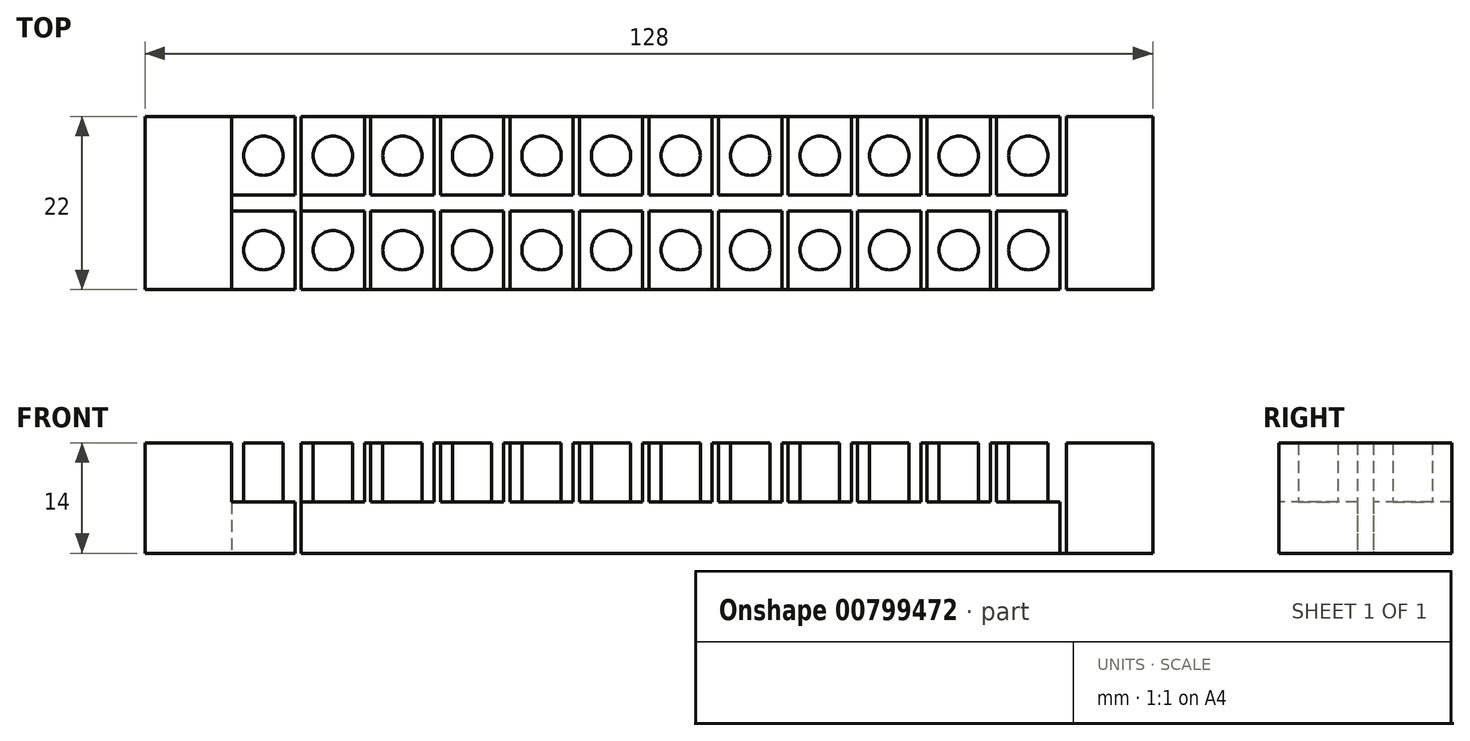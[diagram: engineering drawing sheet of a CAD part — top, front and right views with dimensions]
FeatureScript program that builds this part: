
annotation { "Feature Type Name" : "Feature", "Feature Type Description" : "" }
export const myFeature = defineFeature(function(context is Context, id is Id, definition is map)
    precondition{}
    {
        {
            var Q0;
            Q0=qCreatedBy(makeId("Top.planeOp"),FACE);
            var sketch = newSketch(context, id + "F0", { "sketchPlane" : qUnion([Q0])});
            skLineSegment(sketch, "E0.bottom", {"start": v(0, 0) * mm, "end": v(128, 0) * mm});
            skLineSegment(sketch, "E0.top", {"start": v(0, 22) * mm, "end": v(128, 22) * mm});
            skLineSegment(sketch, "E0.left", {"start": v(0, 0) * mm, "end": v(0, 22) * mm});
            skLineSegment(sketch, "E0.right", {"start": v(128, 0) * mm, "end": v(128, 22) * mm});
            skLineSegment(sketch, "E1", {"start": v(11, 22) * mm, "end": v(11, 0) * mm});
            skLineSegment(sketch, "E2", {"start": v(117, 22) * mm, "end": v(117, 12) * mm});
            skLineSegment(sketch, "E3.0", {"start": v(11, 12) * mm, "end": v(19.03, 12) * mm});
            skLineSegment(sketch, "E4.0", {"start": v(11, 10) * mm, "end": v(19.03, 10) * mm});
            skLineSegment(sketch, "E5.0", {"start": v(19.03, 22) * mm, "end": v(19.03, 12) * mm});
            skCircle(sketch, "E6", {"center": v(15.02, 17) * mm, "radius": 2.5 * mm});
            skLineSegment(sketch, "E7.trimOffspring", {"start": v(19.83, 12) * mm, "end": v(117, 12) * mm});
            skLineSegment(sketch, "E8.trimOffspring", {"start": v(19.03, 10) * mm, "end": v(19.03, 0) * mm});
            skLineSegment(sketch, "E9.trimOffspring", {"start": v(20.63, 10) * mm, "end": v(117, 10) * mm});
            skCircle(sketch, "E10.1.0.0", {"center": v(23.85, 17) * mm, "radius": 2.5 * mm});
            skLineSegment(sketch, "E10.1.0.1", {"start": v(27.87, 22) * mm, "end": v(27.87, 12) * mm});
            skLineSegment(sketch, "E10.1.0.2", {"start": v(19.83, 22) * mm, "end": v(19.83, 12) * mm});
            skCircle(sketch, "E10.2.0.0", {"center": v(32.68, 17) * mm, "radius": 2.5 * mm});
            skLineSegment(sketch, "E10.2.0.1", {"start": v(36.7, 22) * mm, "end": v(36.7, 12) * mm});
            skLineSegment(sketch, "E10.2.0.2", {"start": v(28.67, 22) * mm, "end": v(28.67, 0) * mm});
            skCircle(sketch, "E10.3.0.0", {"center": v(41.52, 17) * mm, "radius": 2.5 * mm});
            skLineSegment(sketch, "E10.3.0.1", {"start": v(45.53, 22) * mm, "end": v(45.53, 12) * mm});
            skLineSegment(sketch, "E10.3.0.2", {"start": v(37.5, 22) * mm, "end": v(37.5, 12) * mm});
            skCircle(sketch, "E10.4.0.0", {"center": v(50.35, 17) * mm, "radius": 2.5 * mm});
            skLineSegment(sketch, "E10.4.0.1", {"start": v(54.37, 22) * mm, "end": v(54.37, 12) * mm});
            skLineSegment(sketch, "E10.4.0.2", {"start": v(46.33, 22) * mm, "end": v(46.33, 12) * mm});
            skCircle(sketch, "E10.5.0.0", {"center": v(59.18, 17) * mm, "radius": 2.5 * mm});
            skLineSegment(sketch, "E10.5.0.1", {"start": v(63.2, 22) * mm, "end": v(63.2, 12) * mm});
            skLineSegment(sketch, "E10.5.0.2", {"start": v(55.17, 22) * mm, "end": v(55.17, 12) * mm});
            skCircle(sketch, "E10.6.0.0", {"center": v(68.01, 17) * mm, "radius": 2.5 * mm});
            skLineSegment(sketch, "E10.6.0.1", {"start": v(72.03, 22) * mm, "end": v(72.03, 12) * mm});
            skLineSegment(sketch, "E10.6.0.2", {"start": v(64, 22) * mm, "end": v(64, 12) * mm});
            skCircle(sketch, "E10.7.0.0", {"center": v(76.85, 17) * mm, "radius": 2.5 * mm});
            skLineSegment(sketch, "E10.7.0.1", {"start": v(80.86, 22) * mm, "end": v(80.86, 12) * mm});
            skLineSegment(sketch, "E10.7.0.2", {"start": v(72.83, 22) * mm, "end": v(72.83, 12) * mm});
            skCircle(sketch, "E10.8.0.0", {"center": v(85.68, 17) * mm, "radius": 2.5 * mm});
            skLineSegment(sketch, "E10.8.0.1", {"start": v(89.7, 22) * mm, "end": v(89.7, 12) * mm});
            skLineSegment(sketch, "E10.8.0.2", {"start": v(81.66, 22) * mm, "end": v(81.66, 12) * mm});
            skCircle(sketch, "E10.9.0.0", {"center": v(94.51, 17) * mm, "radius": 2.5 * mm});
            skLineSegment(sketch, "E10.9.0.1", {"start": v(98.53, 22) * mm, "end": v(98.53, 12) * mm});
            skLineSegment(sketch, "E10.9.0.2", {"start": v(90.5, 22) * mm, "end": v(90.5, 12) * mm});
            skCircle(sketch, "E10.10.0.0", {"center": v(103.35, 17) * mm, "radius": 2.5 * mm});
            skLineSegment(sketch, "E10.10.0.1", {"start": v(107.36, 22) * mm, "end": v(107.36, 12) * mm});
            skLineSegment(sketch, "E10.10.0.2", {"start": v(99.33, 22) * mm, "end": v(99.33, 12) * mm});
            skCircle(sketch, "E10.11.0.0", {"center": v(112.18, 17) * mm, "radius": 2.5 * mm});
            skLineSegment(sketch, "E10.11.0.1", {"start": v(116.2, 22) * mm, "end": v(116.2, 12) * mm});
            skLineSegment(sketch, "E10.11.0.2", {"start": v(108.16, 22) * mm, "end": v(108.16, 12) * mm});
            skLineSegment(sketch, "E10.direction1", {"start": v(11, 0) * mm, "end": v(19.83, 0) * mm, "construction": true});
            skCircle(sketch, "E11", {"center": v(15.02, 5) * mm, "radius": 2.5 * mm});
            skLineSegment(sketch, "E12.1.0.0", {"start": v(19.83, 22) * mm, "end": v(19.83, 0) * mm});
            skCircle(sketch, "E12.1.0.1", {"center": v(23.85, 5) * mm, "radius": 2.5 * mm});
            skLineSegment(sketch, "E12.1.0.2", {"start": v(27.87, 10) * mm, "end": v(27.87, 0) * mm});
            skLineSegment(sketch, "E12.2.0.0", {"start": v(28.67, 22) * mm, "end": v(28.67, 12) * mm});
            skCircle(sketch, "E12.2.0.1", {"center": v(32.68, 5) * mm, "radius": 2.5 * mm});
            skLineSegment(sketch, "E12.2.0.2", {"start": v(36.7, 10) * mm, "end": v(36.7, 0) * mm});
            skLineSegment(sketch, "E13.0.3.0", {"start": v(37.5, 22) * mm, "end": v(37.5, 0) * mm});
            skCircle(sketch, "E13.3.3.0", {"center": v(41.52, 5) * mm, "radius": 2.5 * mm});
            skLineSegment(sketch, "E13.5.3.0", {"start": v(45.53, 10) * mm, "end": v(45.53, 0) * mm});
            skCircle(sketch, "E13.3.4.0", {"center": v(50.35, 5) * mm, "radius": 2.5 * mm});
            skLineSegment(sketch, "E13.5.4.0", {"start": v(54.37, 10) * mm, "end": v(54.37, 0) * mm});
            skCircle(sketch, "E13.3.5.0", {"center": v(59.18, 5) * mm, "radius": 2.5 * mm});
            skLineSegment(sketch, "E13.5.5.0", {"start": v(63.2, 10) * mm, "end": v(63.2, 0) * mm});
            skCircle(sketch, "E13.3.6.0", {"center": v(68.02, 5) * mm, "radius": 2.5 * mm});
            skLineSegment(sketch, "E13.5.6.0", {"start": v(72.03, 10) * mm, "end": v(72.03, 0) * mm});
            skCircle(sketch, "E13.3.7.0", {"center": v(76.85, 5) * mm, "radius": 2.5 * mm});
            skLineSegment(sketch, "E13.5.7.0", {"start": v(80.87, 10) * mm, "end": v(80.87, 0) * mm});
            skLineSegment(sketch, "E13.0.8.0", {"start": v(81.67, 22) * mm, "end": v(81.67, 12) * mm});
            skCircle(sketch, "E13.3.8.0", {"center": v(85.68, 5) * mm, "radius": 2.5 * mm});
            skLineSegment(sketch, "E13.5.8.0", {"start": v(89.7, 10) * mm, "end": v(89.7, 0) * mm});
            skCircle(sketch, "E13.3.9.0", {"center": v(94.52, 5) * mm, "radius": 2.5 * mm});
            skLineSegment(sketch, "E13.5.9.0", {"start": v(98.53, 10) * mm, "end": v(98.53, 0) * mm});
            skCircle(sketch, "E13.3.10.0", {"center": v(103.35, 5) * mm, "radius": 2.5 * mm});
            skLineSegment(sketch, "E13.5.10.0", {"start": v(107.37, 10) * mm, "end": v(107.37, 0) * mm});
            skLineSegment(sketch, "E13.0.11.0", {"start": v(108.17, 22) * mm, "end": v(108.17, 12) * mm});
            skCircle(sketch, "E13.3.11.0", {"center": v(112.18, 5) * mm, "radius": 2.5 * mm});
            skLineSegment(sketch, "E13.5.11.0", {"start": v(116.2, 10) * mm, "end": v(116.2, 0) * mm});
            skLineSegment(sketch, "E14.trimOffspring", {"start": v(19.83, 10) * mm, "end": v(19.83, 0) * mm});
            skLineSegment(sketch, "E15.trimOffspring", {"start": v(28.67, 10) * mm, "end": v(28.67, 0) * mm});
            skLineSegment(sketch, "E16.trimOffspring", {"start": v(37.5, 10) * mm, "end": v(37.5, 0) * mm});
            skLineSegment(sketch, "E17.trimOffspring", {"start": v(46.33, 10) * mm, "end": v(46.33, 0) * mm});
            skLineSegment(sketch, "E18.trimOffspring", {"start": v(55.17, 10) * mm, "end": v(55.17, 0) * mm});
            skLineSegment(sketch, "E19.trimOffspring", {"start": v(117, 10) * mm, "end": v(117, 0) * mm});
            skLineSegment(sketch, "E20.trimOffspring", {"start": v(108.16, 10) * mm, "end": v(108.16, 0) * mm});
            skLineSegment(sketch, "E21.trimOffspring", {"start": v(99.33, 10) * mm, "end": v(99.33, 0) * mm});
            skLineSegment(sketch, "E22.trimOffspring", {"start": v(108.17, 10) * mm, "end": v(108.17, 0) * mm});
            skLineSegment(sketch, "E23.trimOffspring", {"start": v(81.67, 10) * mm, "end": v(81.67, 0) * mm});
            skLineSegment(sketch, "E24.trimOffspring", {"start": v(90.5, 10) * mm, "end": v(90.5, 0) * mm});
            skLineSegment(sketch, "E25.trimOffspring", {"start": v(72.83, 10) * mm, "end": v(72.83, 0) * mm});
            skLineSegment(sketch, "E26.trimOffspring", {"start": v(81.66, 10) * mm, "end": v(81.66, 0) * mm});
            skLineSegment(sketch, "E27.trimOffspring", {"start": v(64, 10) * mm, "end": v(64, 0) * mm});
            skLineSegment(sketch, "E28.trimOffspring", {"start": v(19.83, 10) * mm, "end": v(20.63, 10) * mm});
            skSolve(sketch);
        }
        {
            var Q0;
            {var subQ4=sQuery(id+"F0.wireOp",EDGE,"E0.left");Q0=makeQuery(id+"F0.imprint","IMPRINT",FACE,{"disambiguationData":[TD([[makeQuery(id+"F0.imprint","IMPRINT",EDGE,{"derivedFrom":subQ4}),-1.0]])]});}
            var Q1;
            {var subQ4=sQuery(id+"F0.wireOp",EDGE,"E3.0");Q1=makeQuery(id+"F0.imprint","IMPRINT",FACE,{"disambiguationData":[TD([[makeQuery(id+"F0.imprint","IMPRINT",EDGE,{"derivedFrom":subQ4}),-1.0]])]});}
            var Q2;
            {var subQ0=sQuery(id+"F0.wireOp",EDGE,"E5.0");Q2=makeQuery(id+"F0.imprint","IMPRINT",FACE,{"disambiguationData":[TD([[makeQuery(id+"F0.imprint","IMPRINT",EDGE,{"derivedFrom":subQ0}),1.0]])]});}
            var Q3;
            {var subQ0=sQuery(id+"F0.wireOp",EDGE,"E8.trimOffspring");Q3=makeQuery(id+"F0.imprint","IMPRINT",FACE,{"disambiguationData":[TD([[makeQuery(id+"F0.imprint","IMPRINT",EDGE,{"derivedFrom":subQ0}),1.0]])]});}
            var Q4;
            {var subQ4=sQuery(id+"F0.wireOp",EDGE,"E7.trimOffspring");var subQ5=makeQuery(id+"F0.imprint","INTERSECT",VERTEX,{"derivedFrom":[subQ4,sQuery(id+"F0.wireOp",EDGE,"E10.1.0.1")]});Q4=makeQuery(id+"F0.imprint","IMPRINT",FACE,{"disambiguationData":[TD([[makeQuery(id+"F0.imprint","IMPRINT",EDGE,{"disambiguationData":[TD([[subQ5,1.0]])],"derivedFrom":subQ4}),-1.0]])]});}
            var Q5;
            {var subQ0=sQuery(id+"F0.wireOp",EDGE,"E10.1.0.1");Q5=makeQuery(id+"F0.imprint","IMPRINT",FACE,{"disambiguationData":[TD([[makeQuery(id+"F0.imprint","IMPRINT",EDGE,{"derivedFrom":subQ0}),1.0]])]});}
            var Q6;
            {var subQ3=sQuery(id+"F0.wireOp",EDGE,"E12.1.0.2");Q6=makeQuery(id+"F0.imprint","IMPRINT",FACE,{"disambiguationData":[TD([[makeQuery(id+"F0.imprint","IMPRINT",EDGE,{"derivedFrom":subQ3}),1.0]])]});}
            var Q7;
            {var subQ0=sQuery(id+"F0.wireOp",EDGE,"E7.trimOffspring");var subQ9=makeQuery(id+"F0.imprint","INTERSECT",VERTEX,{"derivedFrom":[subQ0,sQuery(id+"F0.wireOp",EDGE,"E12.2.0.0")]});Q7=makeQuery(id+"F0.imprint","IMPRINT",FACE,{"disambiguationData":[TD([[makeQuery(id+"F0.imprint","IMPRINT",EDGE,{"disambiguationData":[TD([[subQ9,1.0]])],"derivedFrom":subQ0}),-1.0]])]});}
            var Q8;
            {var subQ0=sQuery(id+"F0.wireOp",EDGE,"E10.2.0.1");Q8=makeQuery(id+"F0.imprint","IMPRINT",FACE,{"disambiguationData":[TD([[makeQuery(id+"F0.imprint","IMPRINT",EDGE,{"derivedFrom":subQ0}),1.0]])]});}
            var Q9;
            {var subQ0=sQuery(id+"F0.wireOp",EDGE,"E12.2.0.2");Q9=makeQuery(id+"F0.imprint","IMPRINT",FACE,{"disambiguationData":[TD([[makeQuery(id+"F0.imprint","IMPRINT",EDGE,{"derivedFrom":subQ0}),1.0]])]});}
            var Q10;
            {var subQ4=sQuery(id+"F0.wireOp",EDGE,"E7.trimOffspring");var subQ5=makeQuery(id+"F0.imprint","INTERSECT",VERTEX,{"derivedFrom":[subQ4,sQuery(id+"F0.wireOp",EDGE,"E10.3.0.1")]});Q10=makeQuery(id+"F0.imprint","IMPRINT",FACE,{"disambiguationData":[TD([[makeQuery(id+"F0.imprint","IMPRINT",EDGE,{"disambiguationData":[TD([[subQ5,1.0]])],"derivedFrom":subQ4}),-1.0]])]});}
            var Q11;
            {var subQ0=sQuery(id+"F0.wireOp",EDGE,"E10.3.0.1");Q11=makeQuery(id+"F0.imprint","IMPRINT",FACE,{"disambiguationData":[TD([[makeQuery(id+"F0.imprint","IMPRINT",EDGE,{"derivedFrom":subQ0}),1.0]])]});}
            var Q12;
            {var subQ0=sQuery(id+"F0.wireOp",EDGE,"E13.5.3.0");Q12=makeQuery(id+"F0.imprint","IMPRINT",FACE,{"disambiguationData":[TD([[makeQuery(id+"F0.imprint","IMPRINT",EDGE,{"derivedFrom":subQ0}),1.0]])]});}
            var Q13;
            {var subQ4=sQuery(id+"F0.wireOp",EDGE,"E7.trimOffspring");var subQ5=makeQuery(id+"F0.imprint","INTERSECT",VERTEX,{"derivedFrom":[subQ4,sQuery(id+"F0.wireOp",EDGE,"E10.4.0.1")]});Q13=makeQuery(id+"F0.imprint","IMPRINT",FACE,{"disambiguationData":[TD([[makeQuery(id+"F0.imprint","IMPRINT",EDGE,{"disambiguationData":[TD([[subQ5,1.0]])],"derivedFrom":subQ4}),-1.0]])]});}
            var Q14;
            {var subQ0=sQuery(id+"F0.wireOp",EDGE,"E10.4.0.1");Q14=makeQuery(id+"F0.imprint","IMPRINT",FACE,{"disambiguationData":[TD([[makeQuery(id+"F0.imprint","IMPRINT",EDGE,{"derivedFrom":subQ0}),1.0]])]});}
            var Q15;
            {var subQ0=sQuery(id+"F0.wireOp",EDGE,"E13.5.4.0");Q15=makeQuery(id+"F0.imprint","IMPRINT",FACE,{"disambiguationData":[TD([[makeQuery(id+"F0.imprint","IMPRINT",EDGE,{"derivedFrom":subQ0}),1.0]])]});}
            var Q16;
            {var subQ4=sQuery(id+"F0.wireOp",EDGE,"E7.trimOffspring");var subQ5=makeQuery(id+"F0.imprint","INTERSECT",VERTEX,{"derivedFrom":[subQ4,sQuery(id+"F0.wireOp",EDGE,"E10.5.0.1")]});Q16=makeQuery(id+"F0.imprint","IMPRINT",FACE,{"disambiguationData":[TD([[makeQuery(id+"F0.imprint","IMPRINT",EDGE,{"disambiguationData":[TD([[subQ5,1.0]])],"derivedFrom":subQ4}),-1.0]])]});}
            var Q17;
            {var subQ0=sQuery(id+"F0.wireOp",EDGE,"E10.5.0.1");Q17=makeQuery(id+"F0.imprint","IMPRINT",FACE,{"disambiguationData":[TD([[makeQuery(id+"F0.imprint","IMPRINT",EDGE,{"derivedFrom":subQ0}),1.0]])]});}
            var Q18;
            {var subQ3=sQuery(id+"F0.wireOp",EDGE,"E13.5.5.0");Q18=makeQuery(id+"F0.imprint","IMPRINT",FACE,{"disambiguationData":[TD([[makeQuery(id+"F0.imprint","IMPRINT",EDGE,{"derivedFrom":subQ3}),1.0]])]});}
            var Q19;
            {var subQ3=sQuery(id+"F0.wireOp",EDGE,"E0.right");Q19=makeQuery(id+"F0.imprint","IMPRINT",FACE,{"disambiguationData":[TD([[makeQuery(id+"F0.imprint","IMPRINT",EDGE,{"derivedFrom":subQ3}),1.0]])]});}
            var Q20;
            {var subQ0=sQuery(id+"F0.wireOp",EDGE,"E10.6.0.1");Q20=makeQuery(id+"F0.imprint","IMPRINT",FACE,{"disambiguationData":[TD([[makeQuery(id+"F0.imprint","IMPRINT",EDGE,{"derivedFrom":subQ0}),1.0]])]});}
            var Q21;
            {var subQ0=sQuery(id+"F0.wireOp",EDGE,"E13.5.6.0");Q21=makeQuery(id+"F0.imprint","IMPRINT",FACE,{"disambiguationData":[TD([[makeQuery(id+"F0.imprint","IMPRINT",EDGE,{"derivedFrom":subQ0}),1.0]])]});}
            var Q22;
            {var subQ0=sQuery(id+"F0.wireOp",EDGE,"E10.7.0.1");Q22=makeQuery(id+"F0.imprint","IMPRINT",FACE,{"disambiguationData":[TD([[makeQuery(id+"F0.imprint","IMPRINT",EDGE,{"derivedFrom":subQ0}),1.0]])]});}
            var Q23;
            {var subQ0=sQuery(id+"F0.wireOp",EDGE,"E10.8.0.1");Q23=makeQuery(id+"F0.imprint","IMPRINT",FACE,{"disambiguationData":[TD([[makeQuery(id+"F0.imprint","IMPRINT",EDGE,{"derivedFrom":subQ0}),1.0]])]});}
            var Q24;
            {var subQ0=sQuery(id+"F0.wireOp",EDGE,"E10.9.0.1");Q24=makeQuery(id+"F0.imprint","IMPRINT",FACE,{"disambiguationData":[TD([[makeQuery(id+"F0.imprint","IMPRINT",EDGE,{"derivedFrom":subQ0}),1.0]])]});}
            var Q25;
            {var subQ0=sQuery(id+"F0.wireOp",EDGE,"E13.5.7.0");Q25=makeQuery(id+"F0.imprint","IMPRINT",FACE,{"disambiguationData":[TD([[makeQuery(id+"F0.imprint","IMPRINT",EDGE,{"derivedFrom":subQ0}),1.0]])]});}
            var Q26;
            {var subQ0=sQuery(id+"F0.wireOp",EDGE,"E13.5.8.0");Q26=makeQuery(id+"F0.imprint","IMPRINT",FACE,{"disambiguationData":[TD([[makeQuery(id+"F0.imprint","IMPRINT",EDGE,{"derivedFrom":subQ0}),1.0]])]});}
            var Q27;
            {var subQ0=sQuery(id+"F0.wireOp",EDGE,"E13.5.9.0");Q27=makeQuery(id+"F0.imprint","IMPRINT",FACE,{"disambiguationData":[TD([[makeQuery(id+"F0.imprint","IMPRINT",EDGE,{"derivedFrom":subQ0}),1.0]])]});}
            var Q28;
            {var subQ0=sQuery(id+"F0.wireOp",EDGE,"E13.5.10.0");Q28=makeQuery(id+"F0.imprint","IMPRINT",FACE,{"disambiguationData":[TD([[makeQuery(id+"F0.imprint","IMPRINT",EDGE,{"derivedFrom":subQ0}),1.0]])]});}
            var Q29;
            {var subQ0=sQuery(id+"F0.wireOp",EDGE,"E10.10.0.1");Q29=makeQuery(id+"F0.imprint","IMPRINT",FACE,{"disambiguationData":[TD([[makeQuery(id+"F0.imprint","IMPRINT",EDGE,{"derivedFrom":subQ0}),1.0]])]});}
            extrude(context, id + "F1", {"entities" : qUnion([Q0, Q1, Q2, Q3, Q4, Q5, Q6, Q7, Q8, Q9, Q10, Q11, Q12, Q13, Q14, Q15, Q16, Q17, Q18, Q19, Q20, Q21, Q22, Q23, Q24, Q25, Q26, Q27, Q28, Q29]), "depth" : 14 * mm, "offsetDistance" : 25 * mm});
        }
        {
            var Q0;
            {var subQ1=sQuery(id+"F0.wireOp",EDGE,"E3.0");Q0=makeQuery(id+"F0.imprint","IMPRINT",FACE,{"disambiguationData":[TD([[makeQuery(id+"F0.imprint","IMPRINT",EDGE,{"derivedFrom":subQ1}),1.0]])]});}
            var Q1;
            Q1=makeQuery(id+"F0.imprint","IMPRINT",FACE,{"disambiguationData":[TD([[makeQuery(id+"F0.imprint","IMPRINT",EDGE,{"derivedFrom":sQuery(id+"F0.wireOp",EDGE,"E10.1.0.0")}),-1.0]])]});
            var Q2;
            Q2=makeQuery(id+"F0.imprint","IMPRINT",FACE,{"disambiguationData":[TD([[makeQuery(id+"F0.imprint","IMPRINT",EDGE,{"derivedFrom":sQuery(id+"F0.wireOp",EDGE,"E10.2.0.0")}),-1.0]])]});
            var Q3;
            Q3=makeQuery(id+"F0.imprint","IMPRINT",FACE,{"disambiguationData":[TD([[makeQuery(id+"F0.imprint","IMPRINT",EDGE,{"derivedFrom":sQuery(id+"F0.wireOp",EDGE,"E10.3.0.0")}),-1.0]])]});
            var Q4;
            Q4=makeQuery(id+"F0.imprint","IMPRINT",FACE,{"disambiguationData":[TD([[makeQuery(id+"F0.imprint","IMPRINT",EDGE,{"derivedFrom":sQuery(id+"F0.wireOp",EDGE,"E10.4.0.0")}),-1.0]])]});
            var Q5;
            Q5=makeQuery(id+"F0.imprint","IMPRINT",FACE,{"disambiguationData":[TD([[makeQuery(id+"F0.imprint","IMPRINT",EDGE,{"derivedFrom":sQuery(id+"F0.wireOp",EDGE,"E10.5.0.0")}),-1.0]])]});
            var Q6;
            Q6=makeQuery(id+"F0.imprint","IMPRINT",FACE,{"disambiguationData":[TD([[makeQuery(id+"F0.imprint","IMPRINT",EDGE,{"derivedFrom":sQuery(id+"F0.wireOp",EDGE,"E10.6.0.0")}),-1.0]])]});
            var Q7;
            Q7=makeQuery(id+"F0.imprint","IMPRINT",FACE,{"disambiguationData":[TD([[makeQuery(id+"F0.imprint","IMPRINT",EDGE,{"derivedFrom":sQuery(id+"F0.wireOp",EDGE,"E10.7.0.0")}),-1.0]])]});
            var Q8;
            Q8=makeQuery(id+"F0.imprint","IMPRINT",FACE,{"disambiguationData":[TD([[makeQuery(id+"F0.imprint","IMPRINT",EDGE,{"derivedFrom":sQuery(id+"F0.wireOp",EDGE,"E10.8.0.0")}),-1.0]])]});
            var Q9;
            Q9=makeQuery(id+"F0.imprint","IMPRINT",FACE,{"disambiguationData":[TD([[makeQuery(id+"F0.imprint","IMPRINT",EDGE,{"derivedFrom":sQuery(id+"F0.wireOp",EDGE,"E10.9.0.0")}),-1.0]])]});
            var Q10;
            Q10=makeQuery(id+"F0.imprint","IMPRINT",FACE,{"disambiguationData":[TD([[makeQuery(id+"F0.imprint","IMPRINT",EDGE,{"derivedFrom":sQuery(id+"F0.wireOp",EDGE,"E10.10.0.0")}),-1.0]])]});
            var Q11;
            Q11=makeQuery(id+"F0.imprint","IMPRINT",FACE,{"disambiguationData":[TD([[makeQuery(id+"F0.imprint","IMPRINT",EDGE,{"derivedFrom":sQuery(id+"F0.wireOp",EDGE,"E10.11.0.0")}),-1.0]])]});
            var Q12;
            {var subQ0=sQuery(id+"F0.wireOp",EDGE,"E8.trimOffspring");Q12=makeQuery(id+"F0.imprint","IMPRINT",FACE,{"disambiguationData":[TD([[makeQuery(id+"F0.imprint","IMPRINT",EDGE,{"derivedFrom":subQ0}),-1.0]])]});}
            var Q13;
            {var subQ1=sQuery(id+"F0.wireOp",EDGE,"e5be5b07-9a71-46ae-a25e-6459b5496cdc.trimOffspring");Q13=makeQuery(id+"F0.imprint","IMPRINT",FACE,{"disambiguationData":[TD([[makeQuery(id+"F0.imprint","IMPRINT",EDGE,{"derivedFrom":subQ1}),1.0]])]});}
            var Q14;
            Q14=makeQuery(id+"F0.imprint","IMPRINT",FACE,{"disambiguationData":[TD([[makeQuery(id+"F0.imprint","IMPRINT",EDGE,{"derivedFrom":sQuery(id+"F0.wireOp",EDGE,"E12.2.0.1")}),-1.0]])]});
            var Q15;
            Q15=makeQuery(id+"F0.imprint","IMPRINT",FACE,{"disambiguationData":[TD([[makeQuery(id+"F0.imprint","IMPRINT",EDGE,{"derivedFrom":sQuery(id+"F0.wireOp",EDGE,"E13.3.3.0")}),-1.0]])]});
            var Q16;
            Q16=makeQuery(id+"F0.imprint","IMPRINT",FACE,{"disambiguationData":[TD([[makeQuery(id+"F0.imprint","IMPRINT",EDGE,{"derivedFrom":sQuery(id+"F0.wireOp",EDGE,"E13.3.6.0")}),-1.0]])]});
            var Q17;
            Q17=makeQuery(id+"F0.imprint","IMPRINT",FACE,{"disambiguationData":[TD([[makeQuery(id+"F0.imprint","IMPRINT",EDGE,{"derivedFrom":sQuery(id+"F0.wireOp",EDGE,"E13.3.7.0")}),-1.0]])]});
            var Q18;
            Q18=makeQuery(id+"F0.imprint","IMPRINT",FACE,{"disambiguationData":[TD([[makeQuery(id+"F0.imprint","IMPRINT",EDGE,{"derivedFrom":sQuery(id+"F0.wireOp",EDGE,"E13.3.9.0")}),-1.0]])]});
            var Q19;
            Q19=makeQuery(id+"F0.imprint","IMPRINT",FACE,{"disambiguationData":[TD([[makeQuery(id+"F0.imprint","IMPRINT",EDGE,{"derivedFrom":sQuery(id+"F0.wireOp",EDGE,"E13.3.10.0")}),-1.0]])]});
            var Q20;
            Q20=makeQuery(id+"F0.imprint","IMPRINT",FACE,{"disambiguationData":[TD([[makeQuery(id+"F0.imprint","IMPRINT",EDGE,{"derivedFrom":sQuery(id+"F0.wireOp",EDGE,"E13.3.11.0")}),-1.0]])]});
            var Q21;
            Q21=makeQuery(id+"F0.imprint","IMPRINT",FACE,{"disambiguationData":[TD([[makeQuery(id+"F0.imprint","IMPRINT",EDGE,{"derivedFrom":sQuery(id+"F0.wireOp",EDGE,"E13.3.5.0")}),-1.0]])]});
            var Q22;
            Q22=makeQuery(id+"F0.imprint","IMPRINT",FACE,{"disambiguationData":[TD([[makeQuery(id+"F0.imprint","IMPRINT",EDGE,{"derivedFrom":sQuery(id+"F0.wireOp",EDGE,"E13.3.4.0")}),-1.0]])]});
            var Q23;
            Q23=makeQuery(id+"F0.imprint","IMPRINT",FACE,{"disambiguationData":[TD([[makeQuery(id+"F0.imprint","IMPRINT",EDGE,{"derivedFrom":sQuery(id+"F0.wireOp",EDGE,"E13.3.8.0")}),-1.0]])]});
            var Q24;
            Q24=makeQuery(id+"F0.imprint","IMPRINT",FACE,{"disambiguationData":[TD([[makeQuery(id+"F0.imprint","IMPRINT",EDGE,{"derivedFrom":sQuery(id+"F0.wireOp",EDGE,"E12.1.0.1")}),-1.0]])]});
            extrude(context, id + "F2", {"entities" : qUnion([Q0, Q1, Q2, Q3, Q4, Q5, Q6, Q7, Q8, Q9, Q10, Q11, Q12, Q13, Q14, Q15, Q16, Q17, Q18, Q19, Q20, Q21, Q22, Q23, Q24]), "operationType" : NewBodyOperationType.ADD, "depth" : 6.5 * mm, "offsetDistance" : 25 * mm});
        }
        {
            var Q0;
            Q0=makeQuery(id+"F0.imprint","IMPRINT",FACE,{"disambiguationData":[TD([[makeQuery(id+"F0.imprint","IMPRINT",EDGE,{"derivedFrom":sQuery(id+"F0.wireOp",EDGE,"E6")}),1.0]])]});
            var Q1;
            Q1=makeQuery(id+"F0.imprint","IMPRINT",FACE,{"disambiguationData":[TD([[makeQuery(id+"F0.imprint","IMPRINT",EDGE,{"derivedFrom":sQuery(id+"F0.wireOp",EDGE,"E10.1.0.0")}),1.0]])]});
            var Q2;
            Q2=makeQuery(id+"F0.imprint","IMPRINT",FACE,{"disambiguationData":[TD([[makeQuery(id+"F0.imprint","IMPRINT",EDGE,{"derivedFrom":sQuery(id+"F0.wireOp",EDGE,"E10.2.0.0")}),1.0]])]});
            var Q3;
            Q3=makeQuery(id+"F0.imprint","IMPRINT",FACE,{"disambiguationData":[TD([[makeQuery(id+"F0.imprint","IMPRINT",EDGE,{"derivedFrom":sQuery(id+"F0.wireOp",EDGE,"E10.3.0.0")}),1.0]])]});
            var Q4;
            Q4=makeQuery(id+"F0.imprint","IMPRINT",FACE,{"disambiguationData":[TD([[makeQuery(id+"F0.imprint","IMPRINT",EDGE,{"derivedFrom":sQuery(id+"F0.wireOp",EDGE,"E10.4.0.0")}),1.0]])]});
            var Q5;
            Q5=makeQuery(id+"F0.imprint","IMPRINT",FACE,{"disambiguationData":[TD([[makeQuery(id+"F0.imprint","IMPRINT",EDGE,{"derivedFrom":sQuery(id+"F0.wireOp",EDGE,"E10.5.0.0")}),1.0]])]});
            var Q6;
            Q6=makeQuery(id+"F0.imprint","IMPRINT",FACE,{"disambiguationData":[TD([[makeQuery(id+"F0.imprint","IMPRINT",EDGE,{"derivedFrom":sQuery(id+"F0.wireOp",EDGE,"E10.6.0.0")}),1.0]])]});
            var Q7;
            Q7=makeQuery(id+"F0.imprint","IMPRINT",FACE,{"disambiguationData":[TD([[makeQuery(id+"F0.imprint","IMPRINT",EDGE,{"derivedFrom":sQuery(id+"F0.wireOp",EDGE,"E10.7.0.0")}),1.0]])]});
            var Q8;
            Q8=makeQuery(id+"F0.imprint","IMPRINT",FACE,{"disambiguationData":[TD([[makeQuery(id+"F0.imprint","IMPRINT",EDGE,{"derivedFrom":sQuery(id+"F0.wireOp",EDGE,"E10.8.0.0")}),1.0]])]});
            var Q9;
            Q9=makeQuery(id+"F0.imprint","IMPRINT",FACE,{"disambiguationData":[TD([[makeQuery(id+"F0.imprint","IMPRINT",EDGE,{"derivedFrom":sQuery(id+"F0.wireOp",EDGE,"E10.9.0.0")}),1.0]])]});
            var Q10;
            Q10=makeQuery(id+"F0.imprint","IMPRINT",FACE,{"disambiguationData":[TD([[makeQuery(id+"F0.imprint","IMPRINT",EDGE,{"derivedFrom":sQuery(id+"F0.wireOp",EDGE,"E10.10.0.0")}),1.0]])]});
            var Q11;
            Q11=makeQuery(id+"F0.imprint","IMPRINT",FACE,{"disambiguationData":[TD([[makeQuery(id+"F0.imprint","IMPRINT",EDGE,{"derivedFrom":sQuery(id+"F0.wireOp",EDGE,"E10.11.0.0")}),1.0]])]});
            var Q12;
            Q12=makeQuery(id+"F0.imprint","IMPRINT",FACE,{"disambiguationData":[TD([[makeQuery(id+"F0.imprint","IMPRINT",EDGE,{"derivedFrom":sQuery(id+"F0.wireOp",EDGE,"E11")}),1.0]])]});
            var Q13;
            Q13=makeQuery(id+"F0.imprint","IMPRINT",FACE,{"disambiguationData":[TD([[makeQuery(id+"F0.imprint","IMPRINT",EDGE,{"derivedFrom":sQuery(id+"F0.wireOp",EDGE,"E12.1.0.1")}),1.0]])]});
            var Q14;
            Q14=makeQuery(id+"F0.imprint","IMPRINT",FACE,{"disambiguationData":[TD([[makeQuery(id+"F0.imprint","IMPRINT",EDGE,{"derivedFrom":sQuery(id+"F0.wireOp",EDGE,"E12.2.0.1")}),1.0]])]});
            var Q15;
            Q15=makeQuery(id+"F0.imprint","IMPRINT",FACE,{"disambiguationData":[TD([[makeQuery(id+"F0.imprint","IMPRINT",EDGE,{"derivedFrom":sQuery(id+"F0.wireOp",EDGE,"E13.3.3.0")}),1.0]])]});
            var Q16;
            Q16=makeQuery(id+"F0.imprint","IMPRINT",FACE,{"disambiguationData":[TD([[makeQuery(id+"F0.imprint","IMPRINT",EDGE,{"derivedFrom":sQuery(id+"F0.wireOp",EDGE,"E13.3.4.0")}),1.0]])]});
            var Q17;
            Q17=makeQuery(id+"F0.imprint","IMPRINT",FACE,{"disambiguationData":[TD([[makeQuery(id+"F0.imprint","IMPRINT",EDGE,{"derivedFrom":sQuery(id+"F0.wireOp",EDGE,"E13.3.5.0")}),1.0]])]});
            var Q18;
            Q18=makeQuery(id+"F0.imprint","IMPRINT",FACE,{"disambiguationData":[TD([[makeQuery(id+"F0.imprint","IMPRINT",EDGE,{"derivedFrom":sQuery(id+"F0.wireOp",EDGE,"E13.3.6.0")}),1.0]])]});
            var Q19;
            Q19=makeQuery(id+"F0.imprint","IMPRINT",FACE,{"disambiguationData":[TD([[makeQuery(id+"F0.imprint","IMPRINT",EDGE,{"derivedFrom":sQuery(id+"F0.wireOp",EDGE,"E13.3.7.0")}),1.0]])]});
            var Q20;
            Q20=makeQuery(id+"F0.imprint","IMPRINT",FACE,{"disambiguationData":[TD([[makeQuery(id+"F0.imprint","IMPRINT",EDGE,{"derivedFrom":sQuery(id+"F0.wireOp",EDGE,"E13.3.8.0")}),1.0]])]});
            var Q21;
            Q21=makeQuery(id+"F0.imprint","IMPRINT",FACE,{"disambiguationData":[TD([[makeQuery(id+"F0.imprint","IMPRINT",EDGE,{"derivedFrom":sQuery(id+"F0.wireOp",EDGE,"E13.3.9.0")}),1.0]])]});
            var Q22;
            Q22=makeQuery(id+"F0.imprint","IMPRINT",FACE,{"disambiguationData":[TD([[makeQuery(id+"F0.imprint","IMPRINT",EDGE,{"derivedFrom":sQuery(id+"F0.wireOp",EDGE,"E13.3.10.0")}),1.0]])]});
            var Q23;
            Q23=makeQuery(id+"F0.imprint","IMPRINT",FACE,{"disambiguationData":[TD([[makeQuery(id+"F0.imprint","IMPRINT",EDGE,{"derivedFrom":sQuery(id+"F0.wireOp",EDGE,"E13.3.11.0")}),1.0]])]});
            extrude(context, id + "F3", {"entities" : qUnion([Q0, Q1, Q2, Q3, Q4, Q5, Q6, Q7, Q8, Q9, Q10, Q11, Q12, Q13, Q14, Q15, Q16, Q17, Q18, Q19, Q20, Q21, Q22, Q23]), "operationType" : NewBodyOperationType.ADD, "depth" : 14 * mm, "offsetDistance" : 25 * mm});
        }
    });
